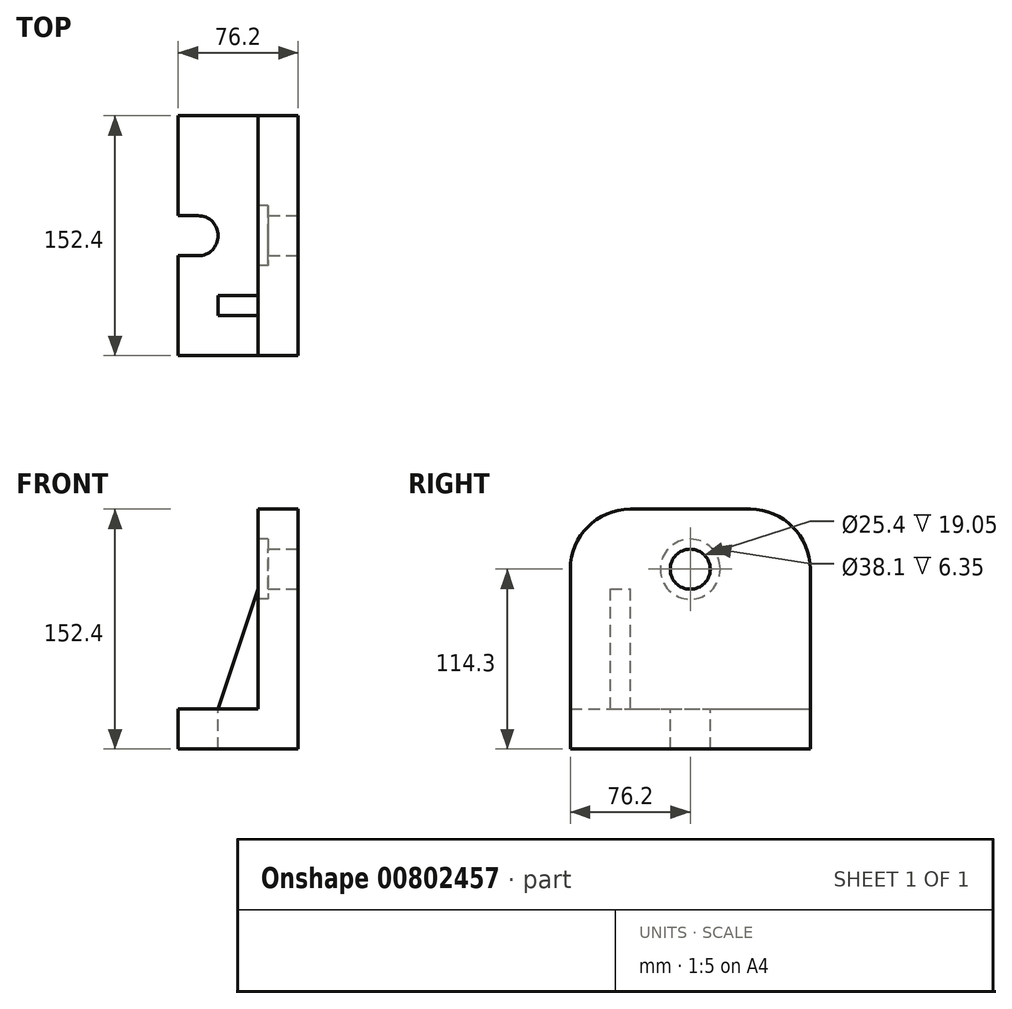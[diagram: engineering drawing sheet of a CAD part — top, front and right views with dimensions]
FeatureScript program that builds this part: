
annotation { "Feature Type Name" : "Feature", "Feature Type Description" : "" }
export const myFeature = defineFeature(function(context is Context, id is Id, definition is map)
    precondition{}
    {
        {
            var Q0;
            Q0=qCreatedBy(makeId("Front.planeOp"),FACE);
            var sketch = newSketch(context, id + "F0", { "sketchPlane" : qUnion([Q0])});
            skLineSegment(sketch, "E0", {"start": v(0, 0) * mm, "end": v(0, 152.4) * mm});
            skLineSegment(sketch, "E1", {"start": v(0, 152.4) * mm, "end": v(-25.4, 152.4) * mm});
            skLineSegment(sketch, "E2", {"start": v(-25.4, 152.4) * mm, "end": v(-25.4, 25.4) * mm});
            skLineSegment(sketch, "E3", {"start": v(-25.4, 25.4) * mm, "end": v(-76.2, 25.4) * mm});
            skLineSegment(sketch, "E4", {"start": v(-76.2, 25.4) * mm, "end": v(-76.2, 0) * mm});
            skLineSegment(sketch, "E5", {"start": v(-76.2, 0) * mm, "end": v(0, 0) * mm});
            skSolve(sketch);
        }
        {
            var Q0;
            Q0=makeQuery(id+"F0.imprint","IMPRINT",FACE,{"disambiguationData":[TD([[makeQuery(id+"F0.imprint","IMPRINT",EDGE,{"derivedFrom":sQuery(id+"F0.wireOp",EDGE,"E0")}),1.0]])]});
            extrude(context, id + "F1", {"entities" : qUnion([Q0]), "endBound" : BoundingType.SYMMETRIC, "depth" : 152.4 * mm, "offsetDistance" : 25.4 * mm});
        }
        {
            var Q0;
            Q0=makeQuery(id+"F1.opExtrude","SWEPT_FACE",FACE,{"disambiguationData":[OSD([sQuery(id+"F0.wireOp",EDGE,"E0")])]});
            var sketch = newSketch(context, id + "F2", { "sketchPlane" : qUnion([Q0])});
            skCircle(sketch, "E6", {"center": v(0, 114.3) * mm, "radius": 12.7 * mm});
            skSolve(sketch);
        }
        {
            var Q0;
            Q0=makeQuery(id+"F2.imprint","IMPRINT",FACE,{"disambiguationData":[TD([[makeQuery(id+"F2.imprint","IMPRINT",EDGE,{"derivedFrom":sQuery(id+"F2.wireOp",EDGE,"E6")}),1.0]])]});
            extrude(context, id + "F3", {"entities" : qUnion([Q0]), "operationType" : NewBodyOperationType.REMOVE, "endBound" : BoundingType.THROUGH_ALL, "oppositeDirection" : true, "depth" : 25.4 * mm, "offsetDistance" : 25.4 * mm});
        }
        {
            var Q0;
            Q0=makeQuery(id+"F1.opExtrude","SWEPT_FACE",FACE,{"disambiguationData":[OSD([sQuery(id+"F0.wireOp",EDGE,"E3")])]});
            var sketch = newSketch(context, id + "F4", { "sketchPlane" : qUnion([Q0])});
            skArc(sketch, "E7", {"start": v(-63.5, -12.7) * mm, "mid": v(-50.8, 0) * mm, "end": v(-63.5, 12.7) * mm});
            skPoint(sketch, "E7.centerSnap0", {"position": v(-76.2, 0) * mm});
            skLineSegment(sketch, "E8", {"start": v(-63.5, 12.7) * mm, "end": v(-76.2, 12.7) * mm});
            skLineSegment(sketch, "E9", {"start": v(-63.5, -12.7) * mm, "end": v(-76.2, -12.7) * mm});
            skSolve(sketch);
        }
        {
            var Q0;
            Q0=makeQuery(id+"F4.imprint","IMPRINT",FACE,{"disambiguationData":[TD([[makeQuery(id+"F4.imprint","IMPRINT",EDGE,{"derivedFrom":sQuery(id+"F4.wireOp",EDGE,"E7")}),1.0]])]});
            extrude(context, id + "F5", {"entities" : qUnion([Q0]), "operationType" : NewBodyOperationType.REMOVE, "endBound" : BoundingType.THROUGH_ALL, "oppositeDirection" : true, "depth" : 25.4 * mm, "offsetDistance" : 25.4 * mm});
        }
        {
            var Q0;
            Q0=makeQuery(id+"F1.opExtrude","CAP_EDGE",EDGE,{"disambiguationData":[OSD([sQuery(id+"F0.wireOp",EDGE,"E1")])],"isStart":false});
            var Q1;
            Q1=makeQuery(id+"F1.opExtrude","CAP_EDGE",EDGE,{"disambiguationData":[OSD([sQuery(id+"F0.wireOp",EDGE,"E1")])],"isStart":true});
            fillet(context, id + "F6", {"entities" : qUnion([Q0, Q1]), "radius" : 38.1 * mm, "tangentPropagation" : true, "allowEdgeOverflow" : false});
        }
        {
            var Q0;
            Q0=makeQuery(id+"F1.opExtrude","SWEPT_FACE",FACE,{"disambiguationData":[OSD([sQuery(id+"F0.wireOp",EDGE,"E2")])]});
            var sketch = newSketch(context, id + "F7", { "sketchPlane" : qUnion([Q0])});
            skCircle(sketch, "E10", {"center": v(0, 114.3) * mm, "radius": 19.05 * mm});
            skSolve(sketch);
        }
        {
            var Q0;
            Q0=makeQuery(id+"F7.imprint","IMPRINT",FACE,{"disambiguationData":[TD([[makeQuery(id+"F7.imprint","IMPRINT",EDGE,{"derivedFrom":sQuery(id+"F7.wireOp",EDGE,"E10")}),1.0]])]});
            extrude(context, id + "F8", {"entities" : qUnion([Q0]), "operationType" : NewBodyOperationType.REMOVE, "oppositeDirection" : true, "depth" : 6.35 * mm, "offsetDistance" : 25.4 * mm});
        }
        {
            var Q0;
            Q0=qCreatedBy(makeId("Front.planeOp"),FACE);
            cPlane(context, id + "F9", {"entities" : qUnion([Q0]), "cplaneType" : CPlaneType.OFFSET, "offset" : 44.45 * mm, "width" : 152.4 * mm, "height" : 152.4 * mm});
        }
        {
            var Q0;
            Q0=qCreatedBy(id+"F9.planeOp",FACE);
            var sketch = newSketch(context, id + "F10", { "sketchPlane" : qUnion([Q0])});
            skPoint(sketch, "E11.0.end.orphan", {"position": v(-76.2, 25.4) * mm});
            skLineSegment(sketch, "E12", {"start": v(-25.4, 25.4) * mm, "end": v(-50.8, 25.4) * mm});
            skLineSegment(sketch, "E13", {"start": v(-25.4, 25.4) * mm, "end": v(-25.4, 101.6) * mm});
            skLineSegment(sketch, "E14", {"start": v(-50.8, 25.4) * mm, "end": v(-25.4, 101.6) * mm});
            skSolve(sketch);
        }
        {
            var Q0;
            Q0=makeQuery(id+"F10.imprint","IMPRINT",FACE,{"disambiguationData":[TD([[makeQuery(id+"F10.imprint","IMPRINT",EDGE,{"derivedFrom":sQuery(id+"F10.wireOp",EDGE,"E12")}),-1.0]])]});
            extrude(context, id + "F11", {"entities" : qUnion([Q0]), "operationType" : NewBodyOperationType.ADD, "endBound" : BoundingType.SYMMETRIC, "depth" : 12.7 * mm, "offsetDistance" : 25.4 * mm});
        }
    });
